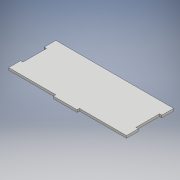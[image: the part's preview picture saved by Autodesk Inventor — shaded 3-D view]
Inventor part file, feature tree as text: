
AUTODESK INVENTOR PART (.ipt)
format: ipt  version: 2017 (Build 210142000, 142)  size: 113,664 bytes
history: native  units: mm
features: extrude x1, sketch x1
ambient origin geometry x8: Origin, YZ Plane, XZ Plane, XY Plane, X Axis, Y Axis, Z Axis, Center Point
bodies: Solid1 (feature_tree)
feature tree (2):
  extrude  "Extrusion1"  Depth=3.0mm TaperAngle=0.0deg
  sketch  "Sketch1"  dims[d10=150.0mm d11=60.0mm d12=3.0mm d13=15.0mm d14=3.0mm d15=30.0mm d16=30.0mm d17=3.0mm d18=3.0mm d19=15.0mm d20=3.0mm d21=0.0mm]
